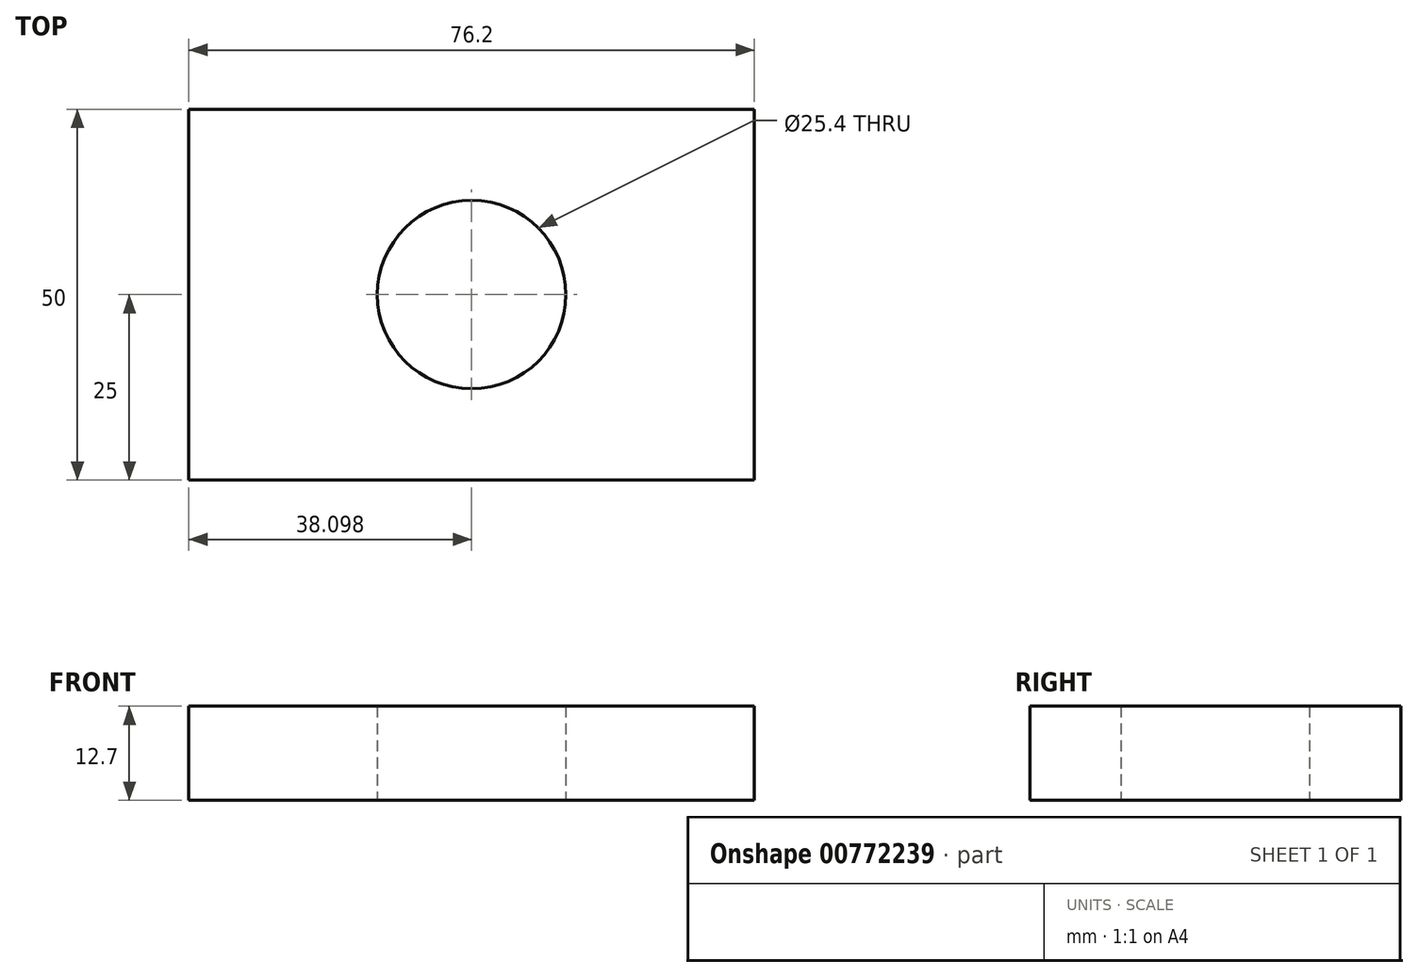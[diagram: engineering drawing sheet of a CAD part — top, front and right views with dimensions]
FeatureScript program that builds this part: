
annotation { "Feature Type Name" : "Feature", "Feature Type Description" : "" }
export const myFeature = defineFeature(function(context is Context, id is Id, definition is map)
    precondition{}
    {
        {
            var Q0;
            Q0=qCreatedBy(makeId("Top.planeOp"),FACE);
            var sketch = newSketch(context, id + "F0", { "sketchPlane" : qUnion([Q0])});
            skLineSegment(sketch, "E0.bottom", {"start": v(81.9, -44.7) * mm, "end": v(-81.9, -44.7) * mm});
            skLineSegment(sketch, "E0.top", {"start": v(81.9, 44.7) * mm, "end": v(-81.9, 44.7) * mm});
            skLineSegment(sketch, "E0.left", {"start": v(81.9, -44.7) * mm, "end": v(81.9, 44.7) * mm});
            skLineSegment(sketch, "E0.right", {"start": v(-81.9, -44.7) * mm, "end": v(-81.9, 44.7) * mm});
            skPoint(sketch, "E0.middle", {"position": v(0, 0) * mm});
            skSolve(sketch);
        }
        {
            var Q0;
            Q0=makeQuery(id+"F0.imprint","IMPRINT",FACE,{"disambiguationData":[TD([[makeQuery(id+"F0.imprint","IMPRINT",EDGE,{"derivedFrom":sQuery(id+"F0.wireOp",EDGE,"E0.bottom")}),-1.0]])]});
            var sketch = newSketch(context, id + "F1", { "sketchPlane" : qUnion([Q0])});
            skLineSegment(sketch, "E1.bottom", {"start": v(-1.76, -9.83) * mm, "end": v(-77.96, -9.83) * mm});
            skLineSegment(sketch, "E1.top", {"start": v(-1.76, 40.17) * mm, "end": v(-77.96, 40.17) * mm});
            skLineSegment(sketch, "E1.left", {"start": v(-1.76, -9.83) * mm, "end": v(-1.76, 40.17) * mm});
            skLineSegment(sketch, "E1.right", {"start": v(-77.96, -9.83) * mm, "end": v(-77.96, 40.17) * mm});
            skPoint(sketch, "E1.middle", {"position": v(-39.86, 15.17) * mm});
            skCircle(sketch, "E2", {"center": v(-39.86, 15.17) * mm, "radius": 12.7 * mm});
            skSolve(sketch);
        }
        {
            var Q0;
            Q0=makeQuery(id+"F1.imprint","IMPRINT",FACE,{"disambiguationData":[TD([[makeQuery(id+"F1.imprint","IMPRINT",EDGE,{"derivedFrom":sQuery(id+"F1.wireOp",EDGE,"E1.bottom")}),-1.0]])]});
            extrude(context, id + "F2", {"entities" : qUnion([Q0]), "depth" : 12.7 * mm, "offsetDistance" : 25.4 * mm});
        }
    });
